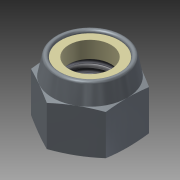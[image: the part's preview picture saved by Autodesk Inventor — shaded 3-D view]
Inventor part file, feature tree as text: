
AUTODESK INVENTOR PART (.ipt)
format: ipt  version: 2013 (Build 170138000, 138)  size: 196,608 bytes
history: native  units: mm (DEFAULTED — no unit token found)
features: sketch x5, extrude x2, revolve x2, other x1, plane x1, thread x1
ambient origin geometry x8: Origin, YZ Plane, XZ Plane, XY Plane, X Axis, Y Axis, Z Axis, Center Point
bodies: Solid1 (feature_tree)
feature tree (12):
  other  "Hexagon_flats_join1"
  extrude  "Extrusion1"  Depth=25.4mm TaperAngle=0.0deg
  revolve  "Revolution1"  Angle=90.0deg
  plane  "Work Plane1"
  extrude  "Extrusion2"  Depth=1.5875mm
  revolve  "Revolution2"  Angle=15.0deg
  thread  "Thread1"  [1 undecoded]
  sketch  "Sketch1"  dims[d0=14.2875mm d3=25.4mm d4=0.0mm]
  sketch  "Sketch2"  dims[d5=13.788101mm d7=90.0deg]
  sketch  "Sketch3"  dims[d9=25.4mm d10=0.0mm d11=1.5875mm]
  sketch  "Sketch4"  dims[d12=15.0deg d13=15.0deg d14=14.2875mm]
  sketch  "Sketch5"  dims[d15=90.0deg d16=25.4mm d17=0.0mm]
note: 1 required parameter value undecoded (feature->parameter linkage not recoverable at this tier; creation-order binding heuristic only, values carry confidence <= 0.55)
